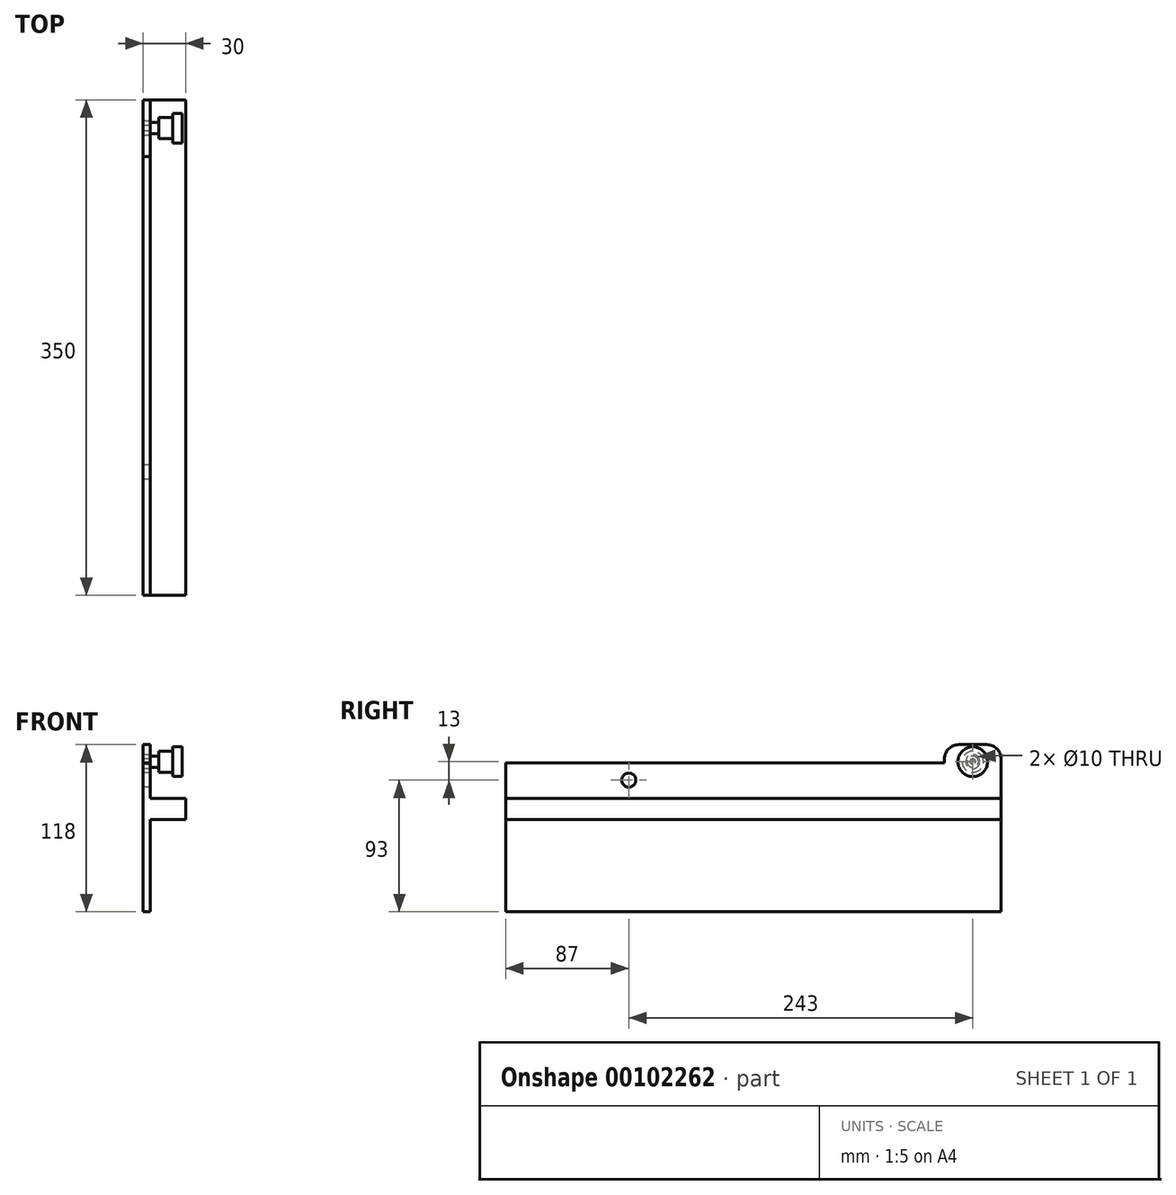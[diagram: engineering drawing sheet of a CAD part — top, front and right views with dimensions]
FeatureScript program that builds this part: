
annotation { "Feature Type Name" : "Feature", "Feature Type Description" : "" }
export const myFeature = defineFeature(function(context is Context, id is Id, definition is map)
    precondition{}
    {
        {
            var Q0;
            Q0=qCreatedBy(makeId("Right.planeOp"),FACE);
            var sketch = newSketch(context, id + "F0", { "sketchPlane" : qUnion([Q0])});
            skLineSegment(sketch, "E0", {"start": v(-330, -1) * mm, "end": v(-20, -1) * mm});
            skLineSegment(sketch, "E1", {"start": v(-20, -1) * mm, "end": v(-20, 2) * mm});
            skLineSegment(sketch, "E2", {"start": v(-10, 12) * mm, "end": v(10, 12) * mm});
            skLineSegment(sketch, "E3", {"start": v(20, 2) * mm, "end": v(20, -106) * mm});
            skLineSegment(sketch, "E4", {"start": v(20, -106) * mm, "end": v(-330, -106) * mm});
            skLineSegment(sketch, "E5", {"start": v(-330, -106) * mm, "end": v(-330, -1) * mm});
            skCircle(sketch, "E6", {"center": v(0, 0) * mm, "radius": 5 * mm});
            skCircle(sketch, "E7", {"center": v(-243, -13) * mm, "radius": 5 * mm});
            skPoint(sketch, "E8.visualSharp", {"position": v(-20, 12) * mm});
            skArc(sketch, "E8.filletArc", {"start": v(-10, 12) * mm, "mid": v(-17.07, 9.07) * mm, "end": v(-20, 2) * mm});
            skPoint(sketch, "E9.visualSharp", {"position": v(20, 12) * mm});
            skArc(sketch, "E9.filletArc", {"start": v(20, 2) * mm, "mid": v(17.07, 9.07) * mm, "end": v(10, 12) * mm});
            skSolve(sketch);
        }
        {
            var Q0;
            Q0=makeQuery(id+"F0.imprint","IMPRINT",FACE,{"disambiguationData":[TD([[makeQuery(id+"F0.imprint","IMPRINT",EDGE,{"derivedFrom":sQuery(id+"F0.wireOp",EDGE,"E0")}),-1.0]])]});
            var Q1;
            Q1=qSketchRegion(id+"F0",true);
            extrude(context, id + "F1", {"entities" : qUnion([Q0, Q1]), "depth" : 5 * mm});
        }
        {
            var Q0;
            Q0=makeQuery(id+"F1.opExtrude","CAP_FACE",FACE,{"disambiguationData":[OSD([sQuery(id+"F0.wireOp",EDGE,"E0"),sQuery(id+"F0.wireOp",EDGE,"E1"),sQuery(id+"F0.wireOp",EDGE,"E2"),sQuery(id+"F0.wireOp",EDGE,"E3"),sQuery(id+"F0.wireOp",EDGE,"E4"),sQuery(id+"F0.wireOp",EDGE,"E5"),sQuery(id+"F0.wireOp",EDGE,"E6"),sQuery(id+"F0.wireOp",EDGE,"E7"),sQuery(id+"F0.wireOp",EDGE,"E8.filletArc"),sQuery(id+"F0.wireOp",EDGE,"E9.filletArc")])],"isStart":false});
            var sketch = newSketch(context, id + "F2", { "sketchPlane" : qUnion([Q0])});
            skLineSegment(sketch, "E10.bottom", {"start": v(-330, -26) * mm, "end": v(20, -26) * mm});
            skLineSegment(sketch, "E10.top", {"start": v(-330, -41) * mm, "end": v(20, -41) * mm});
            skLineSegment(sketch, "E10.left", {"start": v(-330, -26) * mm, "end": v(-330, -41) * mm});
            skLineSegment(sketch, "E10.right", {"start": v(20, -26) * mm, "end": v(20, -41) * mm});
            skSolve(sketch);
        }
        {
            var Q0;
            Q0=qSketchRegion(id+"F2",true);
            extrude(context, id + "F3", {"entities" : qUnion([Q0]), "operationType" : NewBodyOperationType.ADD, "depth" : 25 * mm});
        }
        {
            var Q0;
            Q0=qCreatedBy(makeId("Right.planeOp"),FACE);
            var sketch = newSketch(context, id + "F4", { "sketchPlane" : qUnion([Q0])});
            skCircle(sketch, "E11", {"center": v(0, 0) * mm, "radius": 2 * mm});
            skSolve(sketch);
        }
        {
            var Q0;
            Q0=qSketchRegion(id+"F4",true);
            extrude(context, id + "F5", {"entities" : qUnion([Q0]), "depth" : 5 * mm});
        }
        {
            var Q0;
            Q0=makeQuery(id+"F5.opExtrude","CAP_FACE",FACE,{"disambiguationData":[OSD([sQuery(id+"F4.wireOp",EDGE,"E11")])],"isStart":false});
            var sketch = newSketch(context, id + "F6", { "sketchPlane" : qUnion([Q0])});
            skCircle(sketch, "E12", {"center": v(0, 0) * mm, "radius": 4 * mm});
            skSolve(sketch);
        }
        {
            var Q0;
            Q0=qSketchRegion(id+"F6",true);
            extrude(context, id + "F7", {"entities" : qUnion([Q0]), "operationType" : NewBodyOperationType.ADD, "depth" : 6 * mm});
        }
        {
            var Q0;
            Q0=makeQuery(id+"F7.opExtrude","CAP_FACE",FACE,{"disambiguationData":[OSD([sQuery(id+"F6.wireOp",EDGE,"E12")])],"isStart":false});
            var sketch = newSketch(context, id + "F8", { "sketchPlane" : qUnion([Q0])});
            skCircle(sketch, "E13", {"center": v(0, 0) * mm, "radius": 10.5 * mm});
            skSolve(sketch);
        }
        {
            var Q0;
            Q0=qSketchRegion(id+"F8",true);
            extrude(context, id + "F9", {"entities" : qUnion([Q0]), "operationType" : NewBodyOperationType.ADD, "depth" : 16.5 * mm});
        }
        {
            var Q0;
            Q0=makeQuery(id+"F9.opExtrude","CAP_FACE",FACE,{"disambiguationData":[OSD([sQuery(id+"F8.wireOp",EDGE,"E13")])],"isStart":true});
            var sketch = newSketch(context, id + "F10", { "sketchPlane" : qUnion([Q0])});
            skCircle(sketch, "E14", {"center": v(0, 0) * mm, "radius": 7.5 * mm});
            skCircle(sketch, "E15", {"center": v(0, 0) * mm, "radius": 12.13 * mm});
            skSolve(sketch);
        }
        {
            var Q0;
            Q0=qSketchRegion(id+"F10",true);
            extrude(context, id + "F11", {"entities" : qUnion([Q0]), "operationType" : NewBodyOperationType.REMOVE, "oppositeDirection" : true, "depth" : 10 * mm});
        }
        {
            var Q0;
            Q0=makeQuery(id+"F5.opExtrude","CAP_EDGE",EDGE,{"disambiguationData":[OSD([sQuery(id+"F4.wireOp",EDGE,"E11")])],"isStart":true});
            chamfer(context, id + "F12", {"entities" : qUnion([Q0]), "width" : .3 * mm, "tangentPropagation" : true});
        }
    });
